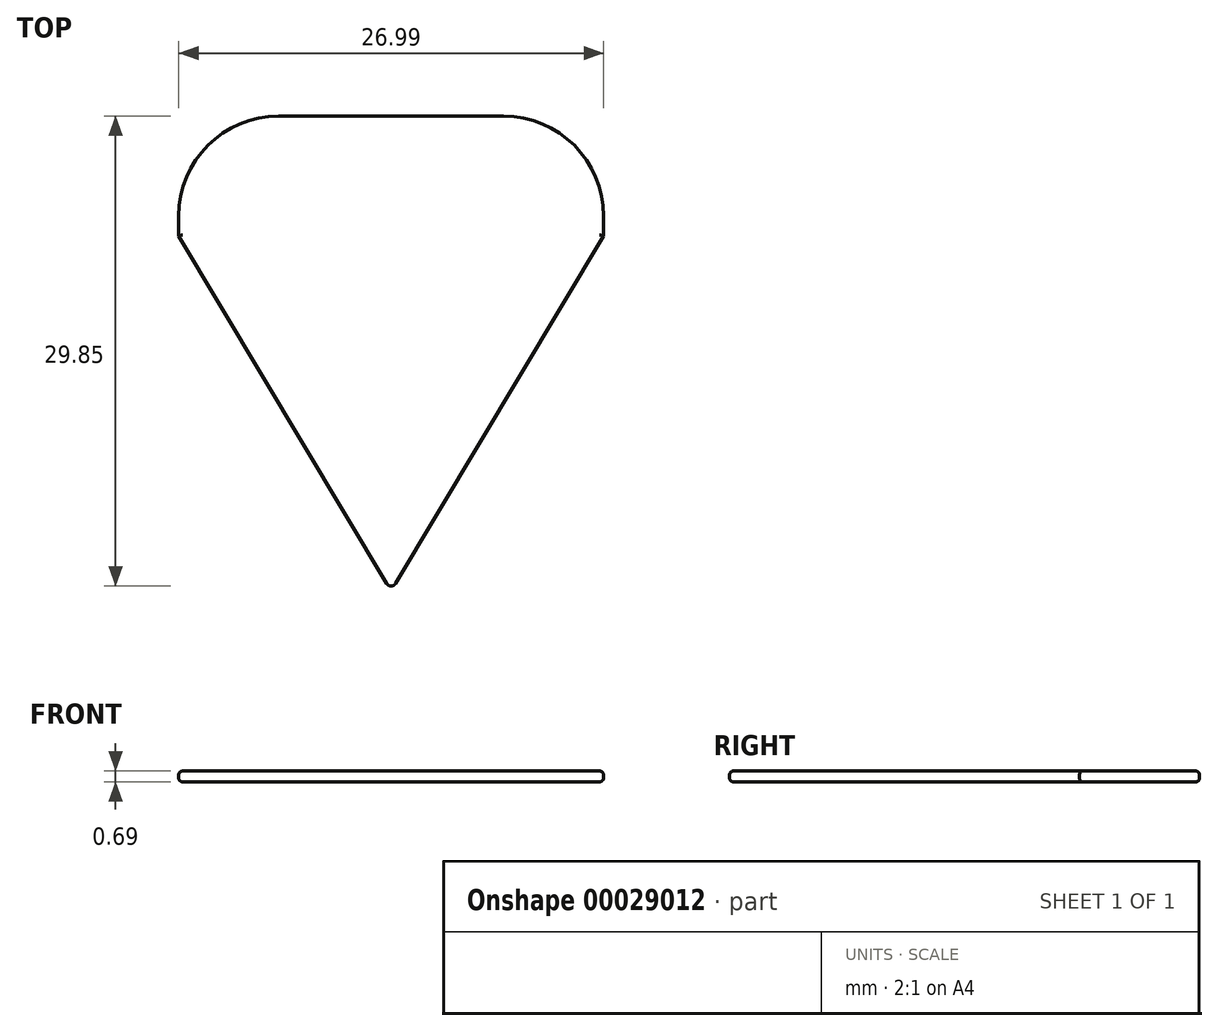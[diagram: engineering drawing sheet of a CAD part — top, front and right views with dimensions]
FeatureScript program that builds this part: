
annotation { "Feature Type Name" : "Feature", "Feature Type Description" : "" }
export const myFeature = defineFeature(function(context is Context, id is Id, definition is map)
    precondition{}
    {
        {
            var Q0;
            Q0=qCreatedBy(makeId("Top.planeOp"),FACE);
            var sketch = newSketch(context, id + "F0", { "sketchPlane" : qUnion([Q0])});
            skLineSegment(sketch, "E0", {"start": v(-29.84, 56.2) * mm, "end": v(-15.55, 56.2) * mm});
            skLineSegment(sketch, "E1", {"start": v(-36.2, 49.85) * mm, "end": v(-36.2, 48.58) * mm});
            skLineSegment(sketch, "E2", {"start": v(-9.2, 48.58) * mm, "end": v(-9.2, 49.85) * mm});
            skLineSegment(sketch, "E3", {"start": v(-22.7, 56.2) * mm, "end": v(-22.7, 26.04) * mm});
            skLineSegment(sketch, "E4", {"start": v(-9.2, 48.58) * mm, "end": v(-22.42, 26.5) * mm});
            skLineSegment(sketch, "E5", {"start": v(-36.2, 48.58) * mm, "end": v(-22.97, 26.5) * mm});
            skPoint(sketch, "E6.visualSharp", {"position": v(-36.2, 56.2) * mm});
            skArc(sketch, "E6.filletArc", {"start": v(-29.84, 56.2) * mm, "mid": v(-34.33, 54.34) * mm, "end": v(-36.2, 49.85) * mm});
            skPoint(sketch, "E7.visualSharp", {"position": v(-9.2, 56.2) * mm});
            skArc(sketch, "E7.filletArc", {"start": v(-9.2, 49.85) * mm, "mid": v(-11.06, 54.34) * mm, "end": v(-15.55, 56.2) * mm});
            skPoint(sketch, "E8.visualSharp", {"position": v(-22.7, 26.04) * mm});
            skArc(sketch, "E8.filletArc", {"start": v(-22.97, 26.5) * mm, "mid": v(-22.7, 26.35) * mm, "end": v(-22.42, 26.5) * mm});
            skSolve(sketch);
        }
        {
            var Q0;
            Q0=makeQuery(id+"F0.imprint","IMPRINT",FACE,{"disambiguationData":[TD([[makeQuery(id+"F0.imprint","IMPRINT",EDGE,{"derivedFrom":sQuery(id+"F0.wireOp",EDGE,"E1")}),1.0]])]});
            var Q1;
            Q1=makeQuery(id+"F0.imprint","IMPRINT",FACE,{"disambiguationData":[TD([[makeQuery(id+"F0.imprint","IMPRINT",EDGE,{"derivedFrom":sQuery(id+"F0.wireOp",EDGE,"E2")}),1.0]])]});
            extrude(context, id + "F1", {"entities" : qUnion([Q0, Q1]), "depth" : 0.69 * mm});
        }
        {
            var Q0;
            Q0=makeQuery(id+"F1.opExtrude","CAP_EDGE",EDGE,{"disambiguationData":[OSD([sQuery(id+"F0.wireOp",EDGE,"E4")])],"isStart":false});
            var Q1;
            Q1=makeQuery(id+"F1.opExtrude","CAP_EDGE",EDGE,{"disambiguationData":[OSD([sQuery(id+"F0.wireOp",EDGE,"E4")])],"isStart":true});
            var Q2;
            Q2=makeQuery(id+"F1.opExtrude","CAP_EDGE",EDGE,{"disambiguationData":[OSD([sQuery(id+"F0.wireOp",EDGE,"E5")])],"isStart":false});
            var Q3;
            Q3=makeQuery(id+"F1.opExtrude","CAP_EDGE",EDGE,{"disambiguationData":[OSD([sQuery(id+"F0.wireOp",EDGE,"E5")])],"isStart":true});
            var Q4;
            Q4=makeQuery(id+"F1.opExtrude","CAP_EDGE",EDGE,{"disambiguationData":[OSD([sQuery(id+"F0.wireOp",EDGE,"E0")])],"isStart":false});
            var Q5;
            Q5=makeQuery(id+"F1.opExtrude","CAP_EDGE",EDGE,{"disambiguationData":[OSD([sQuery(id+"F0.wireOp",EDGE,"E0")])],"isStart":true});
            var Q6;
            Q6=makeQuery(id+"F1.opExtrude","CAP_EDGE",EDGE,{"disambiguationData":[OSD([sQuery(id+"F0.wireOp",EDGE,"E7.filletArc")])],"isStart":false});
            var Q7;
            Q7=makeQuery(id+"F1.opExtrude","CAP_EDGE",EDGE,{"disambiguationData":[OSD([sQuery(id+"F0.wireOp",EDGE,"E7.filletArc")])],"isStart":true});
            var Q8;
            Q8=makeQuery(id+"F1.opExtrude","CAP_EDGE",EDGE,{"disambiguationData":[OSD([sQuery(id+"F0.wireOp",EDGE,"E6.filletArc")])],"isStart":false});
            var Q9;
            Q9=makeQuery(id+"F1.opExtrude","CAP_EDGE",EDGE,{"disambiguationData":[OSD([sQuery(id+"F0.wireOp",EDGE,"E6.filletArc")])],"isStart":true});
            var Q10;
            Q10=makeQuery(id+"F1.opExtrude","CAP_EDGE",EDGE,{"disambiguationData":[OSD([sQuery(id+"F0.wireOp",EDGE,"E1")])],"isStart":false});
            var Q11;
            Q11=makeQuery(id+"F1.opExtrude","CAP_EDGE",EDGE,{"disambiguationData":[OSD([sQuery(id+"F0.wireOp",EDGE,"E2")])],"isStart":false});
            var Q12;
            Q12=makeQuery(id+"F1.opExtrude","CAP_EDGE",EDGE,{"disambiguationData":[OSD([sQuery(id+"F0.wireOp",EDGE,"E1")])],"isStart":true});
            var Q13;
            Q13=makeQuery(id+"F1.opExtrude","CAP_EDGE",EDGE,{"disambiguationData":[OSD([sQuery(id+"F0.wireOp",EDGE,"E2")])],"isStart":true});
            fillet(context, id + "F2", {"entities" : qUnion([Q0, Q1, Q2, Q3, Q4, Q5, Q6, Q7, Q8, Q9, Q10, Q11, Q12, Q13]), "radius" : 0.25 * mm, "tangentPropagation" : true, "allowEdgeOverflow" : false});
        }
    });
